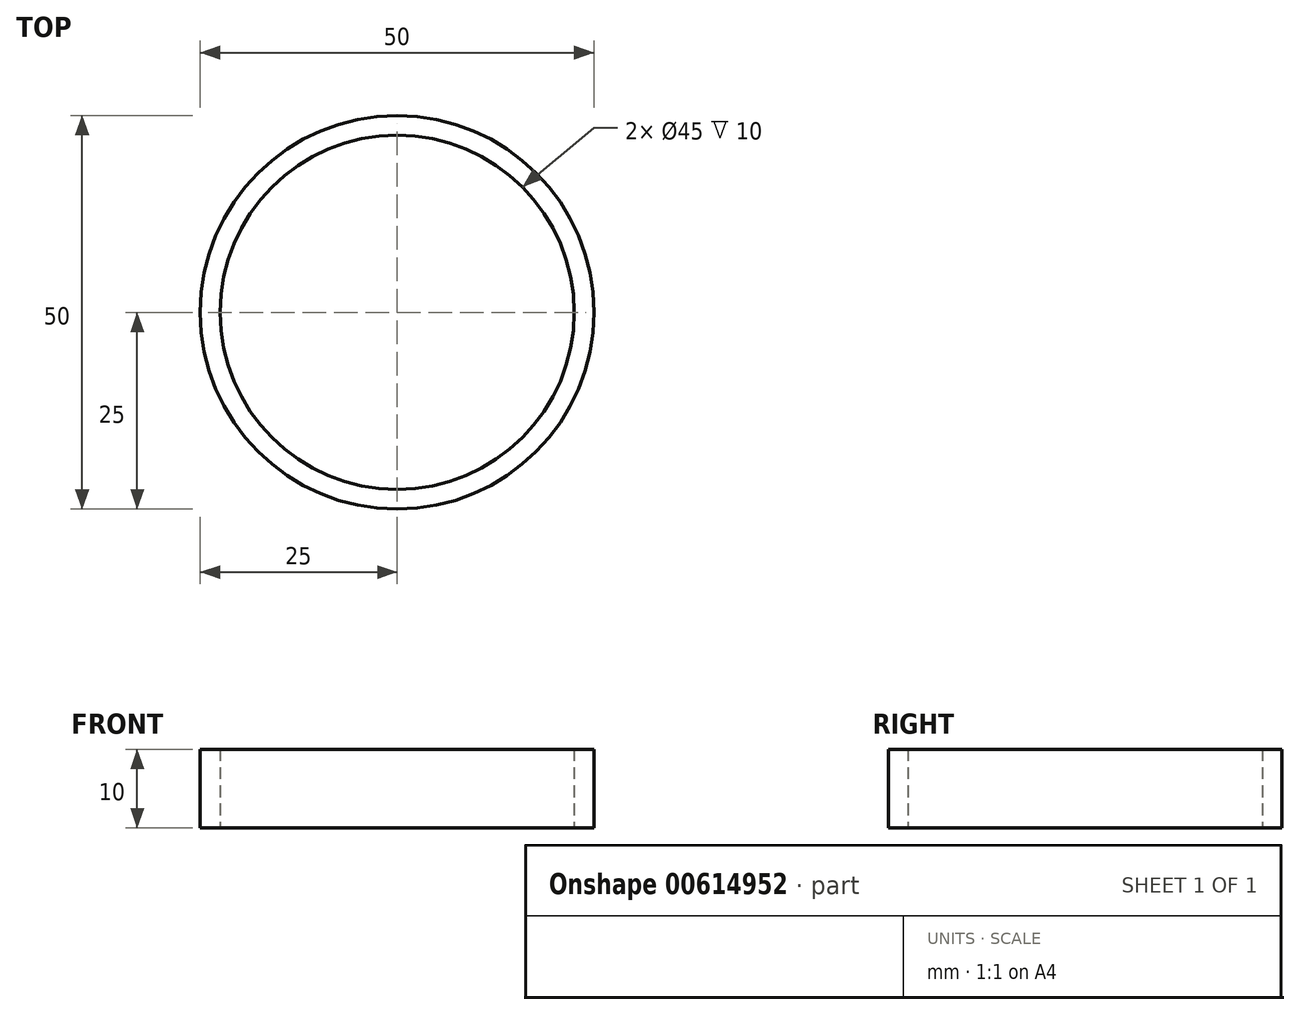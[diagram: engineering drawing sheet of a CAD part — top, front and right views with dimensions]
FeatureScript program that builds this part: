
annotation { "Feature Type Name" : "Feature", "Feature Type Description" : "" }
export const myFeature = defineFeature(function(context is Context, id is Id, definition is map)
    precondition{}
    {
        {
            var Q0;
            Q0=qCreatedBy(makeId("Top.planeOp"),FACE);
            var sketch = newSketch(context, id + "F0", { "sketchPlane" : qUnion([Q0])});
            skCircle(sketch, "E0", {"center": v(0, 0) * mm, "radius": 22.5 * mm});
            skCircle(sketch, "E1", {"center": v(0, 0) * mm, "radius": 25 * mm});
            skSolve(sketch);
        }
        {
            var Q0;
            Q0=makeQuery(id+"F0.imprint","IMPRINT",FACE,{"disambiguationData":[TD([[makeQuery(id+"F0.imprint","IMPRINT",EDGE,{"derivedFrom":sQuery(id+"F0.wireOp",EDGE,"E0")}),-1.0]])]});
            var Q1;
            Q1 = qSketchRegion(id + "F0", true);
            extrude(context, id + "F1", {"entities" : qUnion([Q0, Q1]), "depth" : 10 * mm, "offsetDistance" : 25 * mm});
        }
    });
